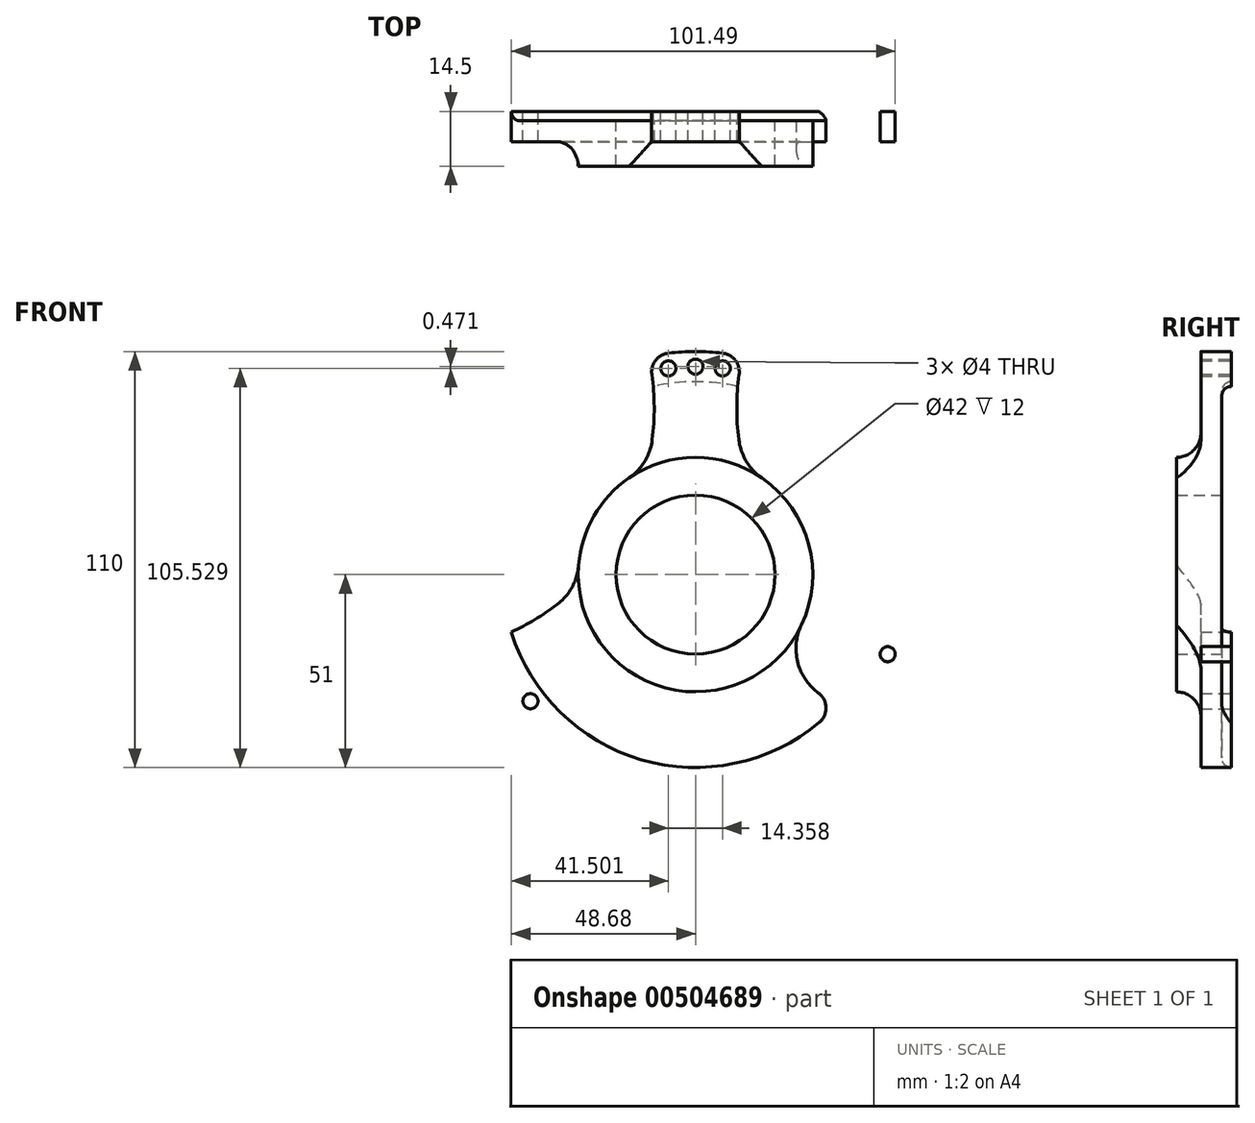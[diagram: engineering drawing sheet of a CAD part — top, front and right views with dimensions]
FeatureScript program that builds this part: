
annotation { "Feature Type Name" : "Feature", "Feature Type Description" : "" }
export const myFeature = defineFeature(function(context is Context, id is Id, definition is map)
    precondition{}
    {
        {
            var Q0;
            Q0=qCreatedBy(makeId("Front.planeOp"),FACE);
            var sketch = newSketch(context, id + "F0", { "sketchPlane" : qUnion([Q0])});
            skCircle(sketch, "E0", {"center": v(0, 0) * mm, "radius": 59 * mm});
            skCircle(sketch, "E1", {"center": v(0, 0) * mm, "radius": 51 * mm});
            skCircle(sketch, "E2", {"center": v(0, 55) * mm, "radius": 2 * mm});
            skCircle(sketch, "E3", {"center": v(7.18, 54.53) * mm, "radius": 2 * mm});
            skLineSegment(sketch, "E4", {"start": v(0, 55) * mm, "end": v(0, 0) * mm});
            skLineSegment(sketch, "E5", {"start": v(7.18, 54.53) * mm, "end": v(0, 0) * mm});
            skCircle(sketch, "E6.MirrorC", {"center": v(-7.18, 54.53) * mm, "radius": 2 * mm});
            skCircle(sketch, "E7.1.0", {"center": v(-43.63, -33.48) * mm, "radius": 2 * mm});
            skCircle(sketch, "E7.1.1", {"center": v(-47.63, -27.5) * mm, "radius": 2 * mm});
            skCircle(sketch, "E7.1.2", {"center": v(-50.81, -21.05) * mm, "radius": 2 * mm});
            skCircle(sketch, "E7.2.0", {"center": v(50.81, -21.05) * mm, "radius": 2 * mm});
            skCircle(sketch, "E7.2.1", {"center": v(47.63, -27.5) * mm, "radius": 2 * mm});
            skCircle(sketch, "E7.2.2", {"center": v(43.63, -33.48) * mm, "radius": 2 * mm});
            skCircle(sketch, "E8", {"center": v(0, 0) * mm, "radius": 21 * mm});
            skArc(sketch, "E9", {"start": v(43.78, -39.56) * mm, "mid": v(0, -22.7) * mm, "end": v(-43.78, -39.56) * mm});
            skLineSegment(sketch, "E10", {"start": v(0, -88) * mm, "end": v(43.78, -39.56) * mm});
            skLineSegment(sketch, "E11", {"start": v(0, -88) * mm, "end": v(-43.78, -39.56) * mm});
            skArc(sketch, "E12.1.0", {"start": v(12.37, 57.69) * mm, "mid": v(19.67, 11.35) * mm, "end": v(56.14, -18.13) * mm});
            skArc(sketch, "E12.2.0", {"start": v(-56.14, -18.13) * mm, "mid": v(-19.67, 11.35) * mm, "end": v(-12.37, 57.69) * mm});
            skCircle(sketch, "E13", {"center": v(0, 0) * mm, "radius": 31 * mm});
            skSolve(sketch);
        }
        {
            var Q0;
            Q0=qCreatedBy(makeId("Right.planeOp"),FACE);
            var sketch = newSketch(context, id + "F1", { "sketchPlane" : qUnion([Q0])});
            skSolve(sketch);
        }
        {
            var Q0;
            Q0 = qSketchRegion(id + "F1", true);
            var Q1;
            Q1=makeQuery(id+"F0.imprint","IMPRINT",FACE,{"disambiguationData":[TD([[makeQuery(id+"F0.imprint","IMPRINT",EDGE,{"derivedFrom":sQuery(id+"F0.wireOp",EDGE,"E2")}),-1.0]])]});
            var Q2;
            {var subQ0=sQuery(id+"F0.wireOp",EDGE,"E4");var subQ1=sQuery(id+"F0.wireOp",EDGE,"E1");var subQ2=makeQuery(id+"F0.imprint","INTERSECT",VERTEX,{"derivedFrom":[subQ1,subQ0]});Q2=makeQuery(id+"F0.imprint","IMPRINT",FACE,{"disambiguationData":[TD([[makeQuery(id+"F0.imprint","IMPRINT",EDGE,{"disambiguationData":[TD([[subQ2,-1.0]])],"derivedFrom":subQ1}),1.0]])]});}
            var Q3;
            {var subQ0=sQuery(id+"F0.wireOp",EDGE,"E5");var subQ1=sQuery(id+"F0.wireOp",EDGE,"E1");var subQ2=makeQuery(id+"F0.imprint","INTERSECT",VERTEX,{"derivedFrom":[subQ1,subQ0]});Q3=makeQuery(id+"F0.imprint","IMPRINT",FACE,{"disambiguationData":[TD([[makeQuery(id+"F0.imprint","IMPRINT",EDGE,{"disambiguationData":[TD([[subQ2,-1.0]])],"derivedFrom":subQ1}),1.0]])]});}
            var Q4;
            {var subQ0=sQuery(id+"F0.wireOp",EDGE,"E5");var subQ1=sQuery(id+"F0.wireOp",EDGE,"E1");var subQ2=makeQuery(id+"F0.imprint","INTERSECT",VERTEX,{"derivedFrom":[subQ1,subQ0]});Q4=makeQuery(id+"F0.imprint","IMPRINT",FACE,{"disambiguationData":[TD([[makeQuery(id+"F0.imprint","IMPRINT",EDGE,{"disambiguationData":[TD([[subQ2,1.0]])],"derivedFrom":subQ1}),1.0]])]});}
            var Q5;
            {var subQ0=sQuery(id+"F0.wireOp",EDGE,"E13");var subQ5=sQuery(id+"F0.wireOp",EDGE,"E4");var subQ12=makeQuery(id+"F0.imprint","INTERSECT",VERTEX,{"derivedFrom":[subQ5,subQ0]});Q5=makeQuery(id+"F0.imprint","IMPRINT",FACE,{"disambiguationData":[TD([[makeQuery(id+"F0.imprint","IMPRINT",EDGE,{"disambiguationData":[TD([[subQ12,-1.0]])],"derivedFrom":subQ5}),-1.0]])]});}
            var Q6;
            {var subQ0=sQuery(id+"F0.wireOp",EDGE,"E13");var subQ1=sQuery(id+"F0.wireOp",EDGE,"E4");var subQ2=makeQuery(id+"F0.imprint","INTERSECT",VERTEX,{"derivedFrom":[subQ1,subQ0]});Q6=makeQuery(id+"F0.imprint","IMPRINT",FACE,{"disambiguationData":[TD([[makeQuery(id+"F0.imprint","IMPRINT",EDGE,{"disambiguationData":[TD([[subQ2,-1.0]])],"derivedFrom":subQ1}),1.0]])]});}
            var Q7;
            {var subQ0=sQuery(id+"F0.wireOp",EDGE,"E13");var subQ1=sQuery(id+"F0.wireOp",EDGE,"E12.2.0");var subQ2=makeQuery(id+"F0.imprint","INTERSECT",VERTEX,{"disambiguationData":[OD(0.0)],"derivedFrom":[subQ1,subQ0]});Q7=makeQuery(id+"F0.imprint","IMPRINT",FACE,{"disambiguationData":[TD([[makeQuery(id+"F0.imprint","IMPRINT",EDGE,{"disambiguationData":[TD([[subQ2,-1.0]])],"derivedFrom":subQ1}),1.0]])]});}
            var Q8;
            {var subQ0=sQuery(id+"F0.wireOp",EDGE,"E13");var subQ1=sQuery(id+"F0.wireOp",EDGE,"E12.1.0");var subQ2=makeQuery(id+"F0.imprint","INTERSECT",VERTEX,{"disambiguationData":[OD(0.0)],"derivedFrom":[subQ1,subQ0]});Q8=makeQuery(id+"F0.imprint","IMPRINT",FACE,{"disambiguationData":[TD([[makeQuery(id+"F0.imprint","IMPRINT",EDGE,{"disambiguationData":[TD([[subQ2,-1.0]])],"derivedFrom":subQ1}),1.0]])]});}
            var Q9;
            {var subQ0=sQuery(id+"F0.wireOp",EDGE,"E13");var subQ1=sQuery(id+"F0.wireOp",EDGE,"E9");var subQ2=makeQuery(id+"F0.imprint","INTERSECT",VERTEX,{"disambiguationData":[OD(0.0)],"derivedFrom":[subQ1,subQ0]});Q9=makeQuery(id+"F0.imprint","IMPRINT",FACE,{"disambiguationData":[TD([[makeQuery(id+"F0.imprint","IMPRINT",EDGE,{"disambiguationData":[TD([[subQ2,-1.0]])],"derivedFrom":subQ1}),1.0]])]});}
            var Q10;
            {var subQ0=sQuery(id+"F0.wireOp",EDGE,"E12.2.0");var subQ1=sQuery(id+"F0.wireOp",EDGE,"E1");var subQ2=makeQuery(id+"F0.imprint","INTERSECT",VERTEX,{"disambiguationData":[OD(1.0)],"derivedFrom":[subQ1,subQ0]});Q10=makeQuery(id+"F0.imprint","IMPRINT",FACE,{"disambiguationData":[TD([[makeQuery(id+"F0.imprint","IMPRINT",EDGE,{"disambiguationData":[TD([[subQ2,-1.0]])],"derivedFrom":subQ1}),1.0]])]});}
            var Q11;
            {var subQ0=sQuery(id+"F0.wireOp",EDGE,"E9");var subQ1=sQuery(id+"F0.wireOp",EDGE,"E1");var subQ2=makeQuery(id+"F0.imprint","INTERSECT",VERTEX,{"disambiguationData":[OD(1.0)],"derivedFrom":[subQ1,subQ0]});Q11=makeQuery(id+"F0.imprint","IMPRINT",FACE,{"disambiguationData":[TD([[makeQuery(id+"F0.imprint","IMPRINT",EDGE,{"disambiguationData":[TD([[subQ2,-1.0]])],"derivedFrom":subQ1}),1.0]])]});}
            var Q12;
            Q12=makeQuery(id+"F0.imprint","IMPRINT",FACE,{"disambiguationData":[TD([[makeQuery(id+"F0.imprint","IMPRINT",EDGE,{"derivedFrom":sQuery(id+"F0.wireOp",EDGE,"E7.2.0")}),1.0]])]});
            var Q13;
            Q13=makeQuery(id+"F0.imprint","IMPRINT",FACE,{"disambiguationData":[TD([[makeQuery(id+"F0.imprint","IMPRINT",EDGE,{"derivedFrom":sQuery(id+"F0.wireOp",EDGE,"E7.1.0")}),1.0]])]});
            extrude(context, id + "F2", {"entities" : qUnion([Q0, Q1, Q2, Q3, Q4, Q5, Q6, Q7, Q8, Q9, Q10, Q11, Q12, Q13]), "depth" : 14.5 * mm});
        }
        {
            var Q0;
            Q0=qCreatedBy(makeId("Right.planeOp"),FACE);
            var sketch = newSketch(context, id + "F3", { "sketchPlane" : qUnion([Q0])});
            skLineSegment(sketch, "E14.bottom", {"start": v(0, 51) * mm, "end": v(0, 51) * mm});
            skLineSegment(sketch, "E14.top", {"start": v(0, 0) * mm, "end": v(-2.5, 0) * mm});
            skLineSegment(sketch, "E14.left", {"start": v(0, 51) * mm, "end": v(0, 0) * mm});
            skLineSegment(sketch, "E14.right", {"start": v(-2.5, 48.5) * mm, "end": v(-2.5, 0) * mm});
            skPoint(sketch, "E15.visualSharp", {"position": v(-2.5, 51) * mm});
            skArc(sketch, "E15.filletArc", {"start": v(0, 51) * mm, "mid": v(-1.77, 50.27) * mm, "end": v(-2.5, 48.5) * mm});
            skLineSegment(sketch, "E16", {"start": v(-8, 59) * mm, "end": v(-8, 37.5) * mm});
            skLineSegment(sketch, "E17", {"start": v(-8, 59) * mm, "end": v(-14.5, 59) * mm});
            skLineSegment(sketch, "E18", {"start": v(-14.5, 59) * mm, "end": v(-14.5, 31) * mm});
            skArc(sketch, "E19.filletArc", {"start": v(-14.5, 31) * mm, "mid": v(-9.9, 32.9) * mm, "end": v(-8, 37.5) * mm});
            skSolve(sketch);
        }
        {
            var Q0;
            Q0 = qSketchRegion(id + "F3", true);
            var Q1;
            Q1=sQuery(id+"F0.wireOp",EDGE,"E0");
            revolve(context, id + "F4", {"operationType" : NewBodyOperationType.REMOVE, "entities" : qUnion([Q0]), "axis" : qUnion([Q1]), "revolveType" : RevolveType.FULL});
        }
        {
            var Q0;
            {var subQ0=sQuery(id+"F0.wireOp",EDGE,"E13");var subQ1=sQuery(id+"F0.wireOp",EDGE,"E12.1.0");Q0=makeQuery(id+"F2.opExtrude","SWEPT_EDGE",EDGE,{"disambiguationData":[OSD([subQ1,subQ0]),TDD([makeQuery(id+"F0.imprint","INTERSECT",VERTEX,{"disambiguationData":[OD(0.0)],"derivedFrom":[subQ1,subQ0]})])]});}
            var Q1;
            {var subQ0=sQuery(id+"F0.wireOp",EDGE,"E13");var subQ1=sQuery(id+"F0.wireOp",EDGE,"E12.1.0");Q1=makeQuery(id+"F2.opExtrude","SWEPT_EDGE",EDGE,{"disambiguationData":[OSD([subQ1,subQ0]),TDD([makeQuery(id+"F0.imprint","INTERSECT",VERTEX,{"disambiguationData":[OD(1.0)],"derivedFrom":[subQ1,subQ0]})])]});}
            var Q2;
            {var subQ0=sQuery(id+"F0.wireOp",EDGE,"E13");var subQ1=sQuery(id+"F0.wireOp",EDGE,"E12.2.0");Q2=makeQuery(id+"F2.opExtrude","SWEPT_EDGE",EDGE,{"disambiguationData":[OSD([subQ1,subQ0]),TDD([makeQuery(id+"F0.imprint","INTERSECT",VERTEX,{"disambiguationData":[OD(0.0)],"derivedFrom":[subQ1,subQ0]})])]});}
            var Q3;
            {var subQ0=sQuery(id+"F0.wireOp",EDGE,"E13");var subQ1=sQuery(id+"F0.wireOp",EDGE,"E12.2.0");Q3=makeQuery(id+"F2.opExtrude","SWEPT_EDGE",EDGE,{"disambiguationData":[OSD([subQ1,subQ0]),TDD([makeQuery(id+"F0.imprint","INTERSECT",VERTEX,{"disambiguationData":[OD(1.0)],"derivedFrom":[subQ1,subQ0]})])]});}
            var Q4;
            {var subQ0=sQuery(id+"F0.wireOp",EDGE,"E13");var subQ1=sQuery(id+"F0.wireOp",EDGE,"E9");Q4=makeQuery(id+"F2.opExtrude","SWEPT_EDGE",EDGE,{"disambiguationData":[OSD([subQ1,subQ0]),TDD([makeQuery(id+"F0.imprint","INTERSECT",VERTEX,{"disambiguationData":[OD(1.0)],"derivedFrom":[subQ1,subQ0]})])]});}
            var Q5;
            {var subQ0=sQuery(id+"F0.wireOp",EDGE,"E13");var subQ1=sQuery(id+"F0.wireOp",EDGE,"E9");Q5=makeQuery(id+"F2.opExtrude","SWEPT_EDGE",EDGE,{"disambiguationData":[OSD([subQ1,subQ0]),TDD([makeQuery(id+"F0.imprint","INTERSECT",VERTEX,{"disambiguationData":[OD(0.0)],"derivedFrom":[subQ1,subQ0]})])]});}
            fillet(context, id + "F5", {"entities" : qUnion([Q0, Q1, Q2, Q3, Q4, Q5]), "radius" : 14.5 * mm, "tangentPropagation" : true, "allowEdgeOverflow" : false});
        }
        {
            var Q0;
            {var subQ0=sQuery(id+"F0.wireOp",EDGE,"E12.1.0");var subQ1=sQuery(id+"F0.wireOp",EDGE,"E0");Q0=makeQuery(id+"F2.opExtrude","SWEPT_EDGE",EDGE,{"disambiguationData":[OSD([subQ1,subQ0]),TDD([makeQuery(id+"F0.imprint","INTERSECT",VERTEX,{"disambiguationData":[OD(0.0)],"derivedFrom":[subQ1,subQ0]})])]});}
            var Q1;
            {var subQ0=sQuery(id+"F0.wireOp",EDGE,"E12.2.0");var subQ1=sQuery(id+"F0.wireOp",EDGE,"E0");Q1=makeQuery(id+"F2.opExtrude","SWEPT_EDGE",EDGE,{"disambiguationData":[OSD([subQ1,subQ0]),TDD([makeQuery(id+"F0.imprint","INTERSECT",VERTEX,{"disambiguationData":[OD(1.0)],"derivedFrom":[subQ1,subQ0]})])]});}
            var Q2;
            {var subQ0=sQuery(id+"F0.wireOp",EDGE,"E12.2.0");var subQ1=sQuery(id+"F0.wireOp",EDGE,"E0");Q2=makeQuery(id+"F2.opExtrude","SWEPT_EDGE",EDGE,{"disambiguationData":[OSD([subQ1,subQ0]),TDD([makeQuery(id+"F0.imprint","INTERSECT",VERTEX,{"disambiguationData":[OD(0.0)],"derivedFrom":[subQ1,subQ0]})])]});}
            var Q3;
            {var subQ0=sQuery(id+"F0.wireOp",EDGE,"E12.1.0");var subQ1=sQuery(id+"F0.wireOp",EDGE,"E0");Q3=makeQuery(id+"F2.opExtrude","SWEPT_EDGE",EDGE,{"disambiguationData":[OSD([subQ1,subQ0]),TDD([makeQuery(id+"F0.imprint","INTERSECT",VERTEX,{"disambiguationData":[OD(1.0)],"derivedFrom":[subQ1,subQ0]})])]});}
            var Q4;
            Q4=makeQuery(id+"F2.opExtrude","SWEPT_EDGE",EDGE,{"disambiguationData":[OSD([sQuery(id+"F0.wireOp",EDGE,"E0"),sQuery(id+"F0.wireOp",EDGE,"E9"),sQuery(id+"F0.wireOp",EDGE,"E11")])]});
            var Q5;
            Q5=makeQuery(id+"F2.opExtrude","SWEPT_EDGE",EDGE,{"disambiguationData":[OSD([sQuery(id+"F0.wireOp",EDGE,"E0"),sQuery(id+"F0.wireOp",EDGE,"E9"),sQuery(id+"F0.wireOp",EDGE,"E10")])]});
            fillet(context, id + "F6", {"entities" : qUnion([Q0, Q1, Q2, Q3, Q4, Q5]), "radius" : 5 * mm, "tangentPropagation" : true, "allowEdgeOverflow" : false});
        }
    });
